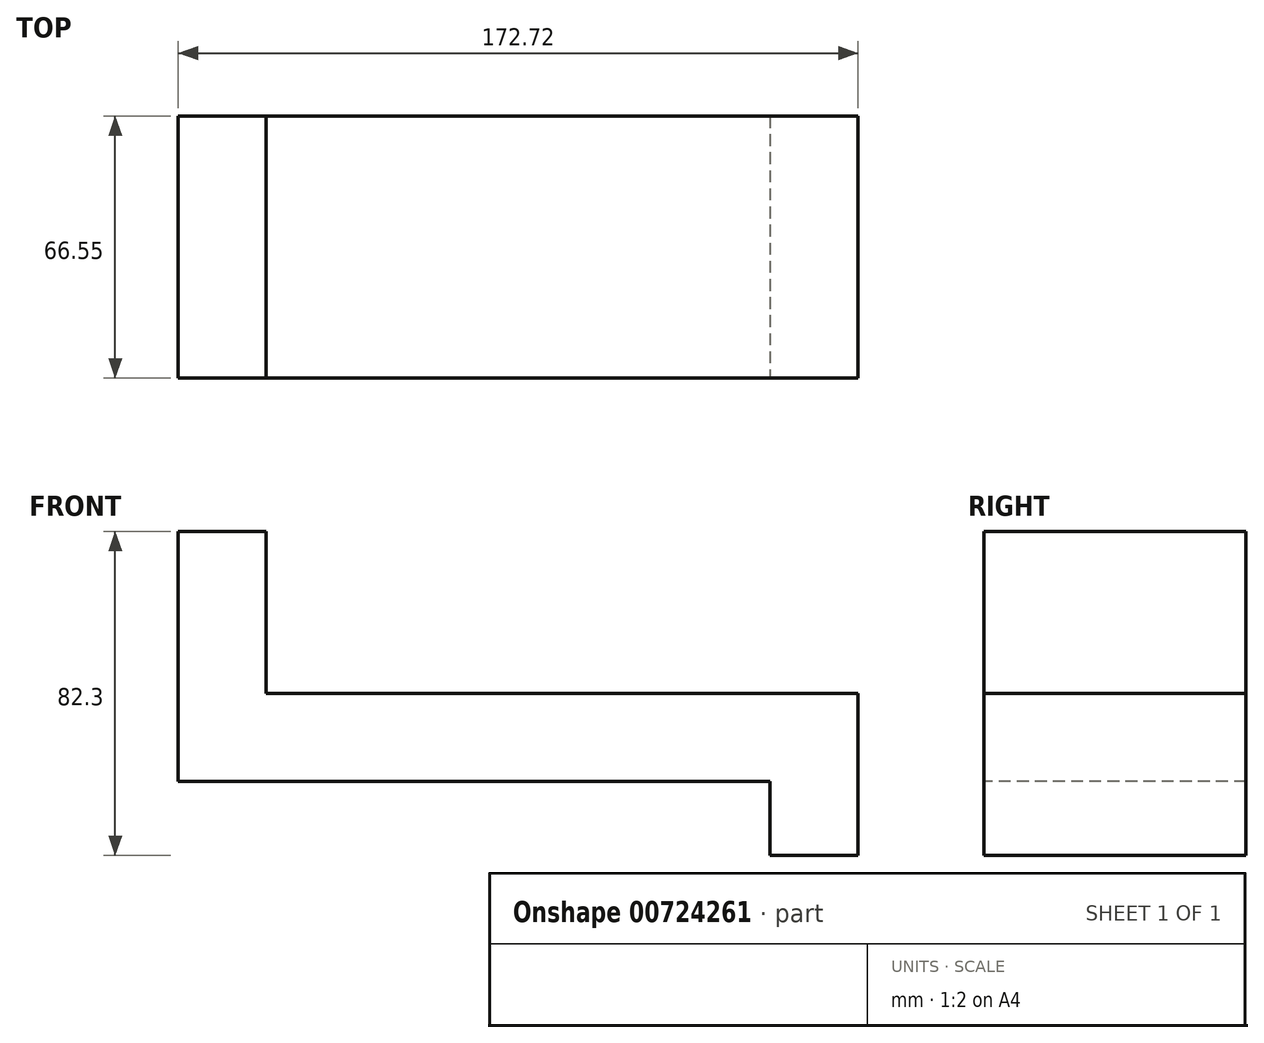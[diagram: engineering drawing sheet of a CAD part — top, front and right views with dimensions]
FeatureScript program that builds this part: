
annotation { "Feature Type Name" : "Feature", "Feature Type Description" : "" }
export const myFeature = defineFeature(function(context is Context, id is Id, definition is map)
    precondition{}
    {
        {
            var Q0;
            Q0=qCreatedBy(makeId("Front.planeOp"),FACE);
            var sketch = newSketch(context, id + "F0", { "sketchPlane" : qUnion([Q0])});
            skLineSegment(sketch, "E0", {"start": v(-69.66, 71.99) * mm, "end": v(-69.66, 8.49) * mm});
            skLineSegment(sketch, "E1", {"start": v(-69.66, 8.49) * mm, "end": v(80.7, 8.49) * mm});
            skLineSegment(sketch, "E2", {"start": v(80.7, 8.49) * mm, "end": v(80.7, -10.3) * mm});
            skLineSegment(sketch, "E3", {"start": v(80.7, -10.3) * mm, "end": v(103.06, -10.3) * mm});
            skLineSegment(sketch, "E4", {"start": v(103.06, -10.3) * mm, "end": v(103.06, 30.84) * mm});
            skLineSegment(sketch, "E5", {"start": v(103.06, 30.84) * mm, "end": v(-47.3, 30.84) * mm});
            skLineSegment(sketch, "E6", {"start": v(-47.3, 30.84) * mm, "end": v(-47.3, 71.99) * mm});
            skLineSegment(sketch, "E7", {"start": v(-69.66, 71.99) * mm, "end": v(-47.3, 71.99) * mm});
            skSolve(sketch);
        }
        {
            var Q0;
            Q0=makeQuery(id+"F0.imprint","IMPRINT",FACE,{"disambiguationData":[TD([[makeQuery(id+"F0.imprint","IMPRINT",EDGE,{"derivedFrom":sQuery(id+"F0.wireOp",EDGE,"E0")}),1.0]])]});
            extrude(context, id + "F1", {"entities" : qUnion([Q0]), "oppositeDirection" : true, "depth" : 66.55 * mm, "offsetDistance" : 25.4 * mm});
        }
    });
